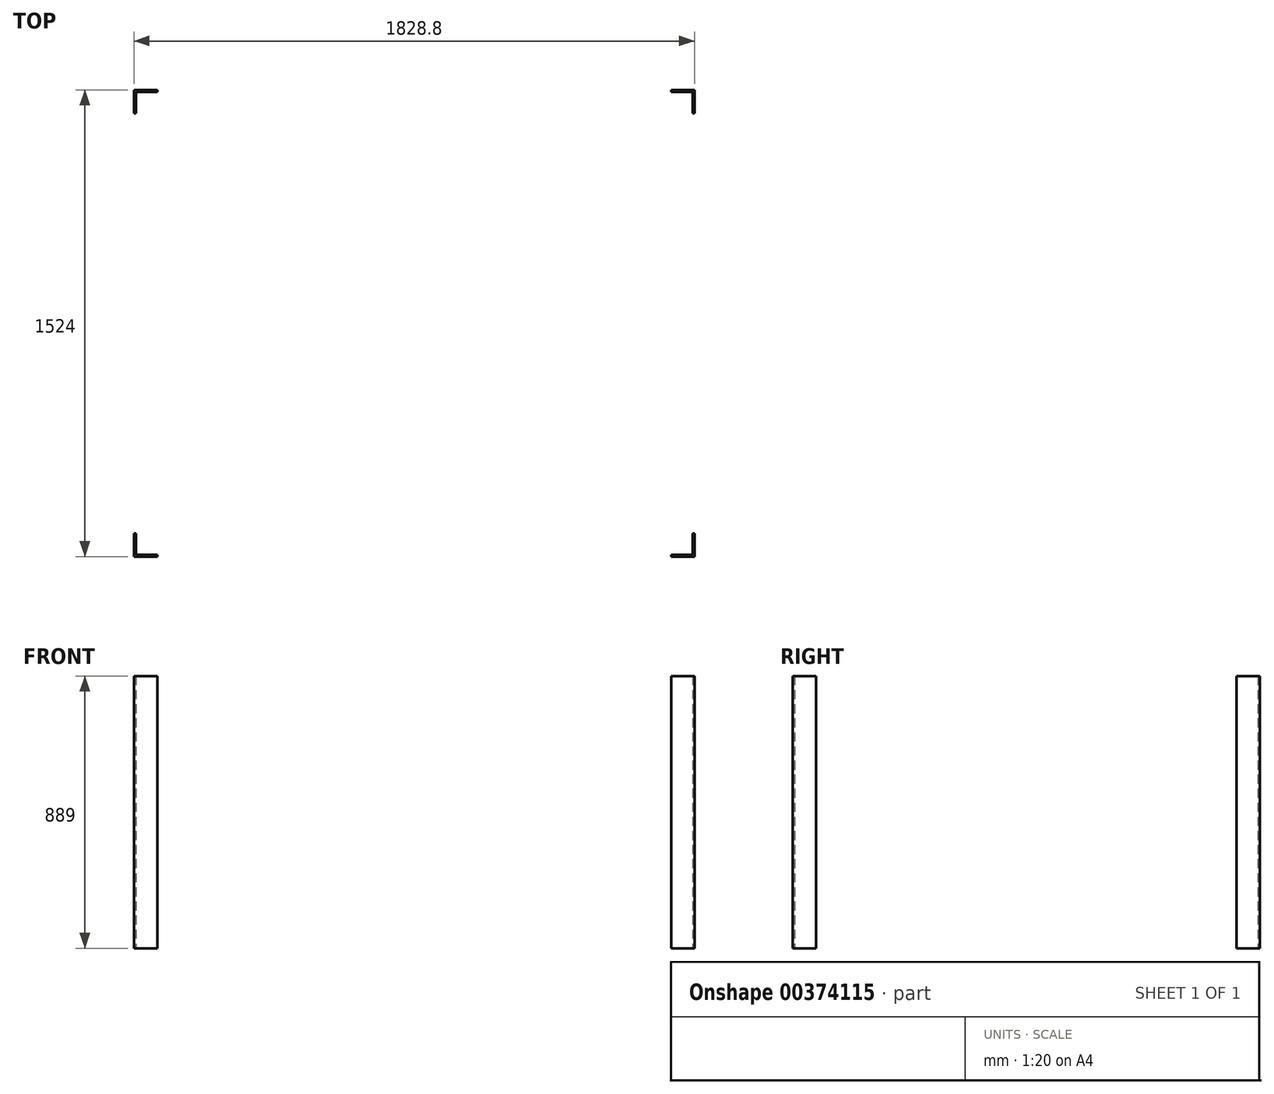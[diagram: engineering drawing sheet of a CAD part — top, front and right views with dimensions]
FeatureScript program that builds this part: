
annotation { "Feature Type Name" : "Feature", "Feature Type Description" : "" }
export const myFeature = defineFeature(function(context is Context, id is Id, definition is map)
    precondition{}
    {
        {
            var Q0;
            Q0=qCreatedBy(makeId("Top.planeOp"),FACE);
            var sketch = newSketch(context, id + "F0", { "sketchPlane" : qUnion([Q0])});
            skPoint(sketch, "E0.middle", {"position": v(0, 0) * mm});
            skLineSegment(sketch, "E1", {"start": v(-914.4, -762) * mm, "end": v(-914.4, -685.8) * mm});
            skLineSegment(sketch, "E2", {"start": v(-914.4, -685.8) * mm, "end": v(-908.05, -685.8) * mm});
            skLineSegment(sketch, "E3", {"start": v(-908.05, -685.8) * mm, "end": v(-908.05, -755.65) * mm});
            skLineSegment(sketch, "E4", {"start": v(-908.05, -755.65) * mm, "end": v(-838.2, -755.65) * mm});
            skLineSegment(sketch, "E5", {"start": v(-838.2, -755.65) * mm, "end": v(-838.2, -762) * mm});
            skLineSegment(sketch, "E6", {"start": v(-838.2, -762) * mm, "end": v(-914.4, -762) * mm});
            skLineSegment(sketch, "E7", {"start": v(0, 0) * mm, "end": v(0, 187.9) * mm, "construction": true});
            skLineSegment(sketch, "E8", {"start": v(152.07, 0) * mm, "end": v(0, 0) * mm, "construction": true});
            skLineSegment(sketch, "E9.MirrorCS", {"start": v(-914.4, 685.8) * mm, "end": v(-908.05, 685.8) * mm});
            skLineSegment(sketch, "E10.MirrorCS", {"start": v(-838.2, 755.65) * mm, "end": v(-838.2, 762) * mm});
            skLineSegment(sketch, "E11.MirrorCS", {"start": v(-908.05, 755.65) * mm, "end": v(-838.2, 755.65) * mm});
            skLineSegment(sketch, "E12.MirrorCS", {"start": v(-914.4, 762) * mm, "end": v(-914.4, 685.8) * mm});
            skLineSegment(sketch, "E13.MirrorCS", {"start": v(-908.05, 685.8) * mm, "end": v(-908.05, 755.65) * mm});
            skLineSegment(sketch, "E14.MirrorCS", {"start": v(-838.2, 762) * mm, "end": v(-914.4, 762) * mm});
            skLineSegment(sketch, "E15.MirrorCS", {"start": v(914.4, -685.8) * mm, "end": v(908.05, -685.8) * mm});
            skLineSegment(sketch, "E16.MirrorCS", {"start": v(914.4, 685.8) * mm, "end": v(908.05, 685.8) * mm});
            skLineSegment(sketch, "E17.MirrorCS", {"start": v(838.2, 755.65) * mm, "end": v(838.2, 762) * mm});
            skLineSegment(sketch, "E18.MirrorCS", {"start": v(838.2, -755.65) * mm, "end": v(838.2, -762) * mm});
            skLineSegment(sketch, "E19.MirrorCS", {"start": v(914.4, -762) * mm, "end": v(914.4, -685.8) * mm});
            skLineSegment(sketch, "E20.MirrorCS", {"start": v(914.4, 762) * mm, "end": v(914.4, 685.8) * mm});
            skLineSegment(sketch, "E21.MirrorCS", {"start": v(908.05, 685.8) * mm, "end": v(908.05, 755.65) * mm});
            skLineSegment(sketch, "E22.MirrorCS", {"start": v(908.05, -685.8) * mm, "end": v(908.05, -755.65) * mm});
            skLineSegment(sketch, "E23.MirrorCS", {"start": v(908.05, 755.65) * mm, "end": v(838.2, 755.65) * mm});
            skLineSegment(sketch, "E24.MirrorCS", {"start": v(908.05, -755.65) * mm, "end": v(838.2, -755.65) * mm});
            skLineSegment(sketch, "E25.MirrorCS", {"start": v(838.2, -762) * mm, "end": v(914.4, -762) * mm});
            skLineSegment(sketch, "E26.MirrorCS", {"start": v(838.2, 762) * mm, "end": v(914.4, 762) * mm});
            skSolve(sketch);
        }
        {
            var Q0;
            Q0 = qSketchRegion(id + "F0", true);
            extrude(context, id + "F1", {"entities" : qUnion([Q0]), "depth" : 889 * mm});
        }
    });
